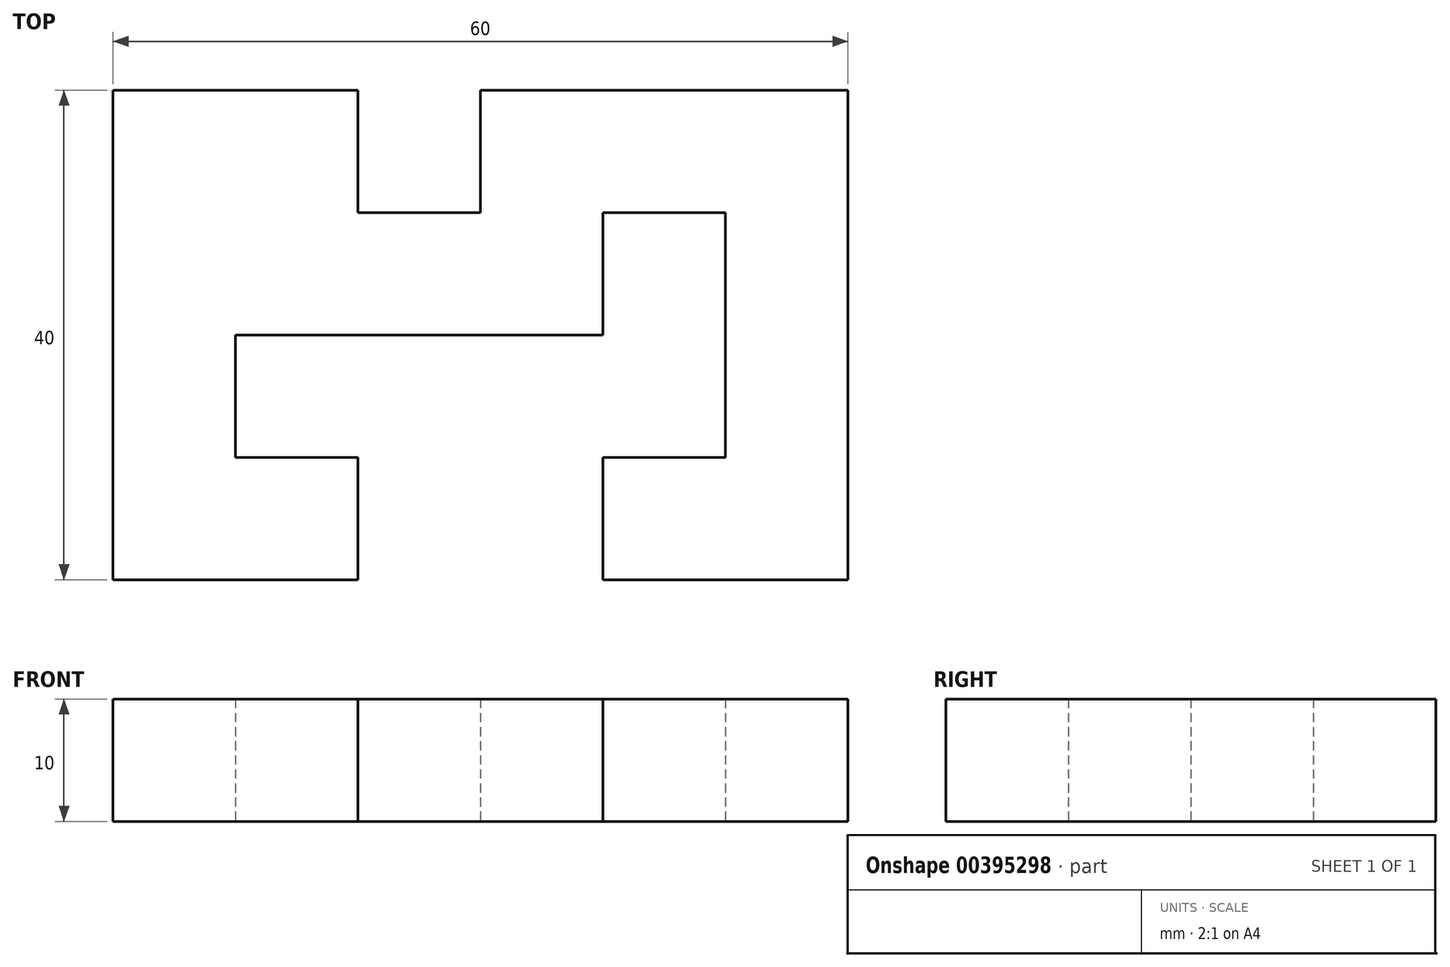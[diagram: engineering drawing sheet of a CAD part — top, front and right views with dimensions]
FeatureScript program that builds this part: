
annotation { "Feature Type Name" : "Feature", "Feature Type Description" : "" }
export const myFeature = defineFeature(function(context is Context, id is Id, definition is map)
    precondition{}
    {
        {
            var Q0;
            Q0=qCreatedBy(makeId("Top.planeOp"),FACE);
            var sketch = newSketch(context, id + "F0", { "sketchPlane" : qUnion([Q0])});
            skLineSegment(sketch, "E0.bottom", {"start": v(-30, 20) * mm, "end": v(30, 20) * mm});
            skLineSegment(sketch, "E0.top", {"start": v(-30, -20) * mm, "end": v(30, -20) * mm});
            skLineSegment(sketch, "E0.left", {"start": v(-30, 20) * mm, "end": v(-30, -20) * mm});
            skLineSegment(sketch, "E0.right", {"start": v(30, 20) * mm, "end": v(30, -20) * mm});
            skPoint(sketch, "E0.middle", {"position": v(0, 0) * mm});
            skLineSegment(sketch, "E1.bottom", {"start": v(-20, 10) * mm, "end": v(20, 10) * mm});
            skLineSegment(sketch, "E1.top", {"start": v(-20, -10) * mm, "end": v(20, -10) * mm});
            skLineSegment(sketch, "E1.left", {"start": v(-20, 10) * mm, "end": v(-20, -10) * mm});
            skLineSegment(sketch, "E1.right", {"start": v(20, 10) * mm, "end": v(20, -10) * mm});
            skLineSegment(sketch, "E2", {"start": v(-20, 0) * mm, "end": v(10, 0) * mm});
            skPoint(sketch, "E2.endSnap0", {"position": v(-20, 0) * mm});
            skLineSegment(sketch, "E3", {"start": v(10, 0) * mm, "end": v(10, 10) * mm});
            skLineSegment(sketch, "E4", {"start": v(0, 20) * mm, "end": v(0, 10) * mm});
            skLineSegment(sketch, "E5", {"start": v(0, 10) * mm, "end": v(-10, 10) * mm});
            skLineSegment(sketch, "E6", {"start": v(-10, 10) * mm, "end": v(-10, 20) * mm});
            skLineSegment(sketch, "E7", {"start": v(-20, -10) * mm, "end": v(-10, -10) * mm});
            skLineSegment(sketch, "E8", {"start": v(-10, -10) * mm, "end": v(-10, -20) * mm});
            skLineSegment(sketch, "E9", {"start": v(0, -10) * mm, "end": v(0, -20) * mm});
            skLineSegment(sketch, "E10", {"start": v(20, -10) * mm, "end": v(10, -10) * mm});
            skLineSegment(sketch, "E11", {"start": v(10, -10) * mm, "end": v(10, -20) * mm});
            skSolve(sketch);
        }
        {
            var Q0;
            {var subQ4=sQuery(id+"F0.wireOp",EDGE,"E0.left");Q0=makeQuery(id+"F0.imprint","IMPRINT",FACE,{"disambiguationData":[TD([[makeQuery(id+"F0.imprint","IMPRINT",EDGE,{"derivedFrom":subQ4}),1.0]])]});}
            var Q1;
            {var subQ3=sQuery(id+"F0.wireOp",EDGE,"E0.right");Q1=makeQuery(id+"F0.imprint","IMPRINT",FACE,{"disambiguationData":[TD([[makeQuery(id+"F0.imprint","IMPRINT",EDGE,{"derivedFrom":subQ3}),-1.0]])]});}
            var Q2;
            {var subQ0=sQuery(id+"F0.wireOp",EDGE,"E2");Q2=makeQuery(id+"F0.imprint","IMPRINT",FACE,{"disambiguationData":[TD([[makeQuery(id+"F0.imprint","IMPRINT",EDGE,{"derivedFrom":subQ0}),1.0]])]});}
            extrude(context, id + "F1", {"entities" : qUnion([Q0, Q1, Q2]), "depth" : 10 * mm});
        }
    });
